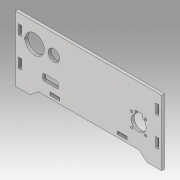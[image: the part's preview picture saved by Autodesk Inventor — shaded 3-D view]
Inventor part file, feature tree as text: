
AUTODESK INVENTOR PART (.ipt)
format: ipt  version: 2019.3 (Build 233278000, 278)  size: 199,168 bytes
history: native  units: mm
features: extrude x3, sketch x3
ambient origin geometry x8: Origin, YZ Plane, XZ Plane, XY Plane, X Axis, Y Axis, Z Axis, Center Point
bodies: Solid1 (feature_tree)
feature tree (6):
  extrude  "Extrusion1"  Depth=10.0mm
  extrude  "Extrusion2"  Depth=10.0mm
  extrude  "Extrusion3"  Depth=36.0mm
  sketch  "Sketch1"  dims[d0=3.0mm d1=10.0mm]
  sketch  "Sketch2"  dims[d2=60.0mm d3=10.0mm]
  sketch  "Sketch3"  dims[d4=152.0mm d5=36.0mm d6=36.0mm d7=3.1mm d8=10.0mm d9=20.0mm d10=5.0mm d11=10.0mm d12=3.0mm d13=3.0mm d14=3.0mm d15=15.0mm d16=15.0mm d17=105.0mm d18=3.0mm d19=0.0mm d21=16.0mm d24=10.0mm d25=0.0mm d26=22.4mm d29=1.0mm d30=6.58mm d31=9.83mm d32=15.5mm d33=7.0mm d34=18.0mm d35=2.5mm d36=17.0mm d37=17.0mm d38=10.253048mm d39=10.253048mm d40=10.253048mm d41=17.75mm d42=10.0mm d43=17.75mm d44=12.0mm d45=20.0mm d46=20.0mm d47=20.0mm d48=2.0mm d49=10.8mm d50=20.0mm d51=10.050126mm d52=10.0mm d53=0.0mm]
